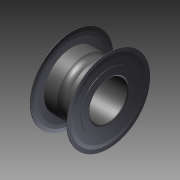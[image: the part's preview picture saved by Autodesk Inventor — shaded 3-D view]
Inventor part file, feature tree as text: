
AUTODESK INVENTOR PART (.ipt)
format: ipt  version: 2011 SP1 (Build 150282100, 282)  size: 179,200 bytes
history: native  units: mm
features: revolve x3, sketch x3
ambient origin geometry x8: Origin, YZ Plane, XZ Plane, XY Plane, X Axis, Y Axis, Z Axis, Center Point
bodies: Solid1 (feature_tree)
feature tree (6):
  revolve  "Revolution1"  Angle=360.0deg
  revolve  "Revolution2"  [1 undecoded]
  revolve  "Revolution3"  [1 undecoded]
  sketch  "Sketch_13"  dims[d0=360.0deg d1=360.0deg]
  sketch  "Sketch_25"  dims[d2=360.0deg]
  sketch  "Sketch_26"
note: 2 required parameter values undecoded (feature->parameter linkage not recoverable at this tier; creation-order binding heuristic only, values carry confidence <= 0.55)
